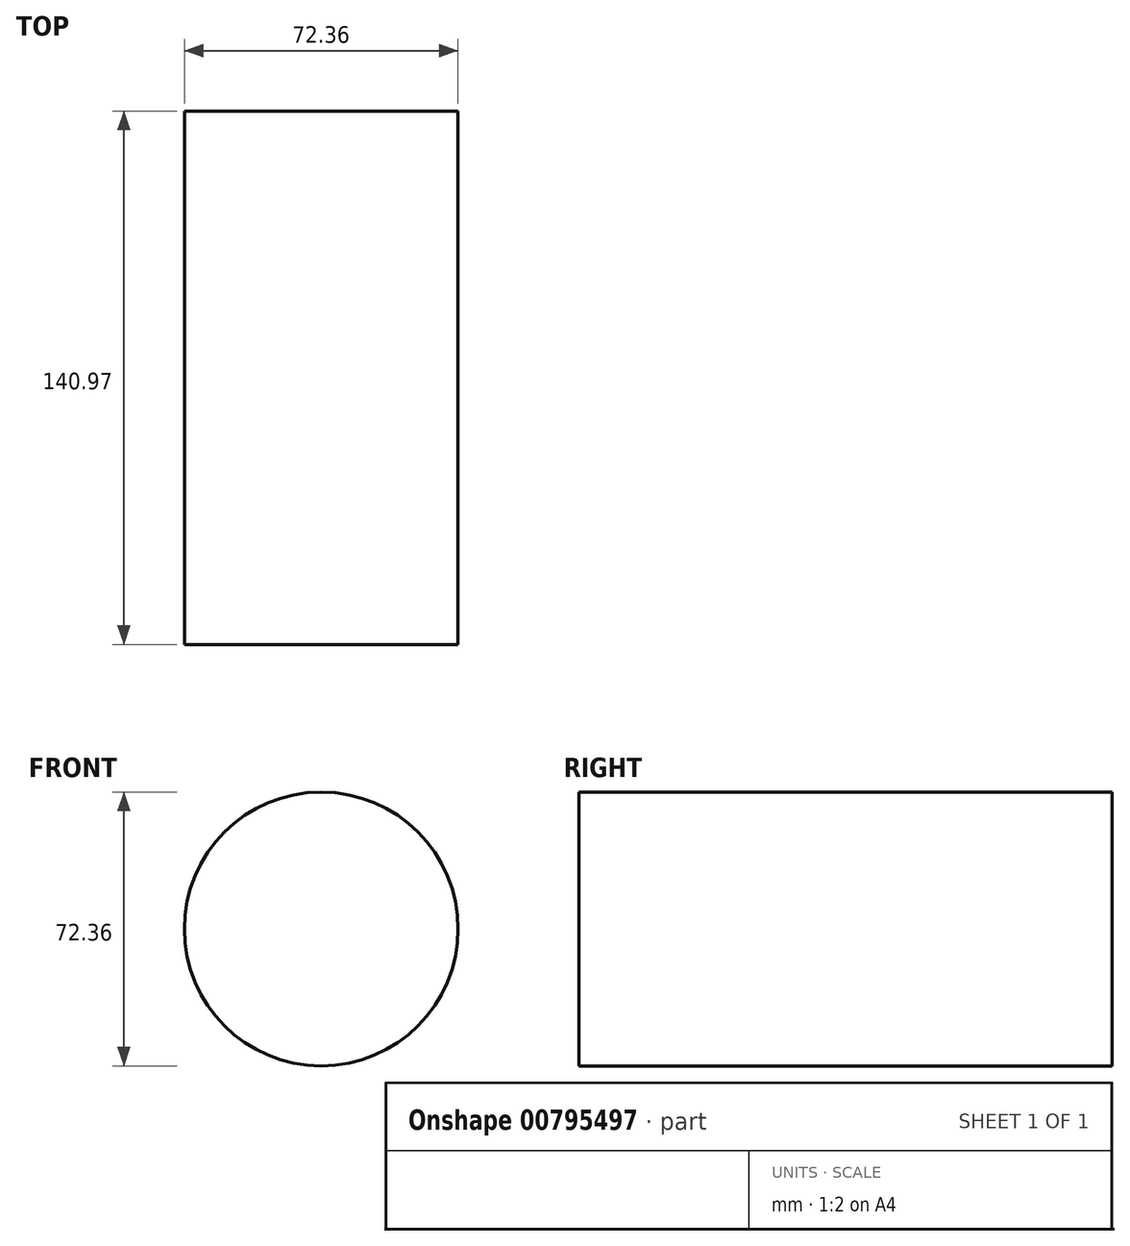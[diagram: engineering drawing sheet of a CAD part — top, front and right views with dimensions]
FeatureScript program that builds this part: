
annotation { "Feature Type Name" : "Feature", "Feature Type Description" : "" }
export const myFeature = defineFeature(function(context is Context, id is Id, definition is map)
    precondition{}
    {
        {
            var Q0;
            Q0=qCreatedBy(makeId("Front.planeOp"),FACE);
            var sketch = newSketch(context, id + "F0", { "sketchPlane" : qUnion([Q0])});
            skCircle(sketch, "E0", {"center": v(-101.3, 34.88) * mm, "radius": 36.18 * mm});
            skSolve(sketch);
        }
        {
            var Q0;
            Q0=makeQuery(id+"F0.imprint","IMPRINT",FACE,{"disambiguationData":[TD([[makeQuery(id+"F0.imprint","IMPRINT",EDGE,{"derivedFrom":sQuery(id+"F0.wireOp",EDGE,"E0")}),1.0]])]});
            extrude(context, id + "F1", {"entities" : qUnion([Q0]), "depth" : 25.4 * mm, "offsetDistance" : 25.4 * mm});
        }
        {
            var Q0;
            Q0=makeQuery(id+"F1.opExtrude","CAP_FACE",FACE,{"disambiguationData":[OSD([sQuery(id+"F0.wireOp",EDGE,"E0")])],"isStart":false});
            var Q1;
            Q1=makeQuery(id+"F1.opExtrude","CAP_FACE",FACE,{"disambiguationData":[OSD([sQuery(id+"F0.wireOp",EDGE,"E0")])],"isStart":true});
            extrude(context, id + "F2", {"entities" : qUnion([Q0, Q1]), "operationType" : NewBodyOperationType.ADD, "depth" : 25.4 * mm, "offsetDistance" : 25.4 * mm});
        }
        {
            var Q0;
            {var subQ0=sQuery(id+"F0.wireOp",EDGE,"E0");Q0=makeQuery(id+"F2.opExtrude","CAP_FACE",FACE,{"disambiguationData":[OSD([subQ0]),TDD([makeQuery(id+"F1.opExtrude","CAP_FACE",FACE,{"disambiguationData":[OSD([subQ0])],"isStart":false})])],"isStart":false});}
            var Q1;
            Q1=makeQuery(id+"F1.opExtrude","CAP_FACE",FACE,{"disambiguationData":[OSD([sQuery(id+"F0.wireOp",EDGE,"E0")])],"isStart":true});
            extrude(context, id + "F3", {"entities" : qUnion([Q0, Q1]), "operationType" : NewBodyOperationType.ADD, "depth" : 90.17 * mm, "offsetDistance" : 25.4 * mm});
        }
    });
